# Revit family: Hager-GAMMA-Surface_mounted-IP30-Without_Cover-Without_DIN-Hosted-FR-fr
name_source: partatom
category: Electrical Equipment
units: mm (PartAtom-declared; Revit-internal decimal feet)

## family parameters
Cut with Voids When Loaded = No
Host = Face
Maintain Annotation Orientation = Yes
Panel Configuration = Two Columns, Circuits Across
Part Type = Panelboard
Room Calculation Point = No
Round Connector Dimension = Use Diameter
Shared = No

## types (1)
- GAMMA-Surface_mounted_W250_H250_D103_13_Modular_Spacing-GD113A
    BC_MODEL_ID = 1554289
    BC_OBJECT_ID = 513855
    BC_OBJECT_VERSION = #3
    BC_VARIANT_ID = 1178801
    Code hager = ADD-EC000214_EU
    Default Elevation = 0 mm  [stored 0 ft]
    EF000003 - mode de pose = saillie
    EF000008 - largeur = 250 mm  [stored 0.82021 ft]
    EF000024 - résistant aux UV = No
    EF000040 - hauteur = 250 mm  [stored 0.82021 ft]
    EF000049 - profondeur = 103 mm  [stored 0.337927 ft]
    EF000116 - numéro RAL = 9010
    EF000118 - avec cadre/support de montage = No
    EF000218 - profondeur d'encastrement = 0 mm  [stored 0 ft]
    EF000266 - nombre de rangées = 1
    EF000332 - hauteur d'encastrement = 0 mm  [stored 0 ft]
    EF000846 - largeur d'encastrement = 0 mm  [stored 0 ft]
    EF001062 - finition CEM = No
    EF001088 - possibilité de montage en saillie = No
    EF001131 - profondeur intérieure = 0 mm  [stored 0 ft]
    EF001134 - rail DIN = No
    EF002950 - largeur en nombre de modules = 13
    EF004462 - type de fermeture = autre
    EF005474 - indice de protection (IP) = IP30
    EF006244 - couvercle/porte transparent(e) = No
    EF006306 - avec serrure = No
    EF015776 - borne de mise à la terre = Yes
    EF015777 - borne à conducteur neutre = Yes
    EF015941 - porte pour transmission du signal = Yes
    ETIM class code = EC000214
    ETIM class name = Small distribution board
    HG000001-nombre de colonnes = 1
    HG000002-avec porte = No
    HG000003-Gamme = GAMMA
    HG000004-Référence fabricant = GD113A
    HG000005-Epaisseur = 2 mm  [stored 0.00656168 ft]
    HG000006-Encastré = No
    HG000007-Nombre de colonnes vides = 0
    HG000008-Nombre de rangées vides = 0
    HG000009-Porte à double battant = No
    HG000010-Portes asymétriques = No
    HG000011-Rangées du bas vides = No
    HG000012-Angle de pivotement de la porte = 90.00°
    HG000013-Porte à gauche = No
    HG000014-Porte à droite = Yes
    HG000015-Visibilité de l'emprise de la porte = Yes
    HG000016-Visibilité de la porte 3D = Yes
    HG000017-Distance entre pôles = 18 mm  [stored 0.0590551 ft]
    HG000060-RAL-number = 9010
    HG000099-ID modèle Onfly = 507532
    HGEF000266-Nombre de rangées = 1
    HGEF0002950-largeur en nombre de modules = 13
    Manufacturer = Hager
    Name = GAMMA-Surface_mounted-IP30-Without_Cover-Without_DIN-FR
    Name BIM&CO = Electricity
    Name hager = ADD_Enclosures_EC000214
    Reference = GAMMA-Surface_mounted_W250_H250_D103_13_Modular_Spacing-GD113A
    Uniformat = Low Tension Service & Dist.
    Uniformat code = D501001

note: [stored X ft] marks values corroborated as IEEE doubles in the binary element streams (Revit-internal decimal feet)

## geometry (parser evidence)
native form markers: Sweep x14
no freeform markers — native parametric forms only
